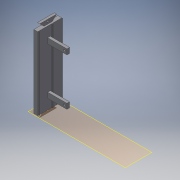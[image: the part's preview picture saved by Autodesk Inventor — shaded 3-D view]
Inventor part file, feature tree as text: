
AUTODESK INVENTOR PART (.ipt)
format: ipt  version: 2016 SP2 (Build 200236200, 236)  size: 203,776 bytes
history: native  units: mm
features: reference x13, extrude x7, sketch x7, plane x1
ambient origin geometry x8: Origin, YZ Plane, XZ Plane, XY Plane, X Axis, Y Axis, Z Axis, Center Point
bodies: Volumenkörper1 (feature_tree)
feature tree (28):
  plane  "Arbeitsebene1"
  extrude  "Extrusion1"  Depth=4.4mm TaperAngle=0.0deg
  extrude  "Extrusion2"  Depth=6.0mm
  extrude  "Extrusion3"  Depth=1.0mm
  sketch  "Skizze4"  dims[d9=2.0mm d10=10.0mm]
  extrude  "Extrusion4"  Depth=10.0mm
  extrude  "Extrusion5"  Depth=5.0mm
  extrude  "Extrusion6"  Depth=80.0mm
  extrude  "Extrusion7"  Depth=36.75mm TaperAngle=0.0deg
  sketch  "Skizze1"  dims[d0=138.8mm d1=0.0mm d2=4.4mm d3=0.0mm]
  reference  "Referenz1"
  reference  "Referenz2"
  reference  "Referenz3"
  reference  "Referenz4"
  reference  "Referenz5"
  reference  "Referenz6"
  reference  "Referenz7"
  reference  "Referenz8"
  reference  "Referenz9"
  sketch  "Skizze2"  dims[d4=6.0mm d5=6.0mm]
  reference  "Referenz10"
  reference  "Referenz11"
  reference  "Referenz12"
  reference  "Referenz13"
  sketch  "Skizze3"  dims[d6=3.5mm d7=0.0mm d8=1.0mm]
  sketch  "Skizze5"  dims[d11=5.0mm d12=5.0mm]
  sketch  "Skizze6"  dims[d13=10.0mm d14=80.0mm]
  sketch  "Skizze7"  dims[d15=2.0mm d16=36.75mm d17=0.0mm d18=1.0mm d19=0.0mm d20=3.5mm d21=3.5mm d22=5.0mm d23=5.0mm d24=5.0mm d25=5.0mm d26=10.0mm d27=0.0mm d28=5.8mm d29=5.8mm d30=2.5mm d31=0.0mm]
